# Revit family: Light_Fixture-Wall_Sconce-KOHLER-Holt-K-38414_1
name_source: partatom
category: Lighting Fixtures
units: mm (PartAtom-declared; Revit-internal decimal feet)

## family parameters
Cut with Voids When Loaded = No
Host = Face
Light Source = Yes
OmniClass Number = 23.35.47.11
OmniClass Title = Lighting Fixtures
Part Type = Normal
Room Calculation Point = No
Round Connector Dimension = Use Diameter
Shared = No

## types (3) — shared parameters
ADA Compliant = No
Apparent Load = 180 VA
Assembly Code = D5040.50
Color Filter = 16777215
Date Modified = 04/05/2023
Default Elevation = 60"
Description = Madera Globe 3-Light Sconce
Dimming Lamp Color Temperature Shift = Incandescent Lamp Curve
Electrical Connector = Yes
Electrical Note = One Dedicated Cicuit Required
Hardware Included = No
Height = 9 3/4"
Lamp = 3*E26 Type A 60W
Length = 23 15/16"
Light Source Symbol Size = 3"
Manufacturer = Kohler Co.
Master Format 2014 = 26 51 13
Master Format 2014 Name = Interior Lighting Fixtures, Lamps, And Ballasts
Material = Premium Metal Construction
Product Documentation Link = https://www.us.kohler.com
Product Name = Holt
Product Page URL = http://www.us.kohler.com
URL = https://www.us.kohler.com
Voltage = 120 V
WaterSense Certified = No
Wattage Comments = 180 W
Width = 6 13/16"

## per-type parameters (varying)
| type | Finish | Model | Secondary Finish | Tube Finish | Type |
| CPL-Polished Chrome | KOHLER-Metal-CPL-Polished_Chrome | K-38414-SC03-CPL | KOHLER-Metal-CPL-Polished_Chrome | Kohler-Wood-WSW-White_Stain_Wood | 1 |
| BNL-Brushed Nickel | KOHLER-Metal-BNL-Brushed_Nickel | K-38414-SC03-BNL | KOHLER-Metal-BNL-Brushed_Nickel | Kohler-Wood-1WE-Terry_Walnut | 2 |
| BML-Matte Black With Brushed Modern Brass | KOHLER-Metal-BLL-Matte_Black | K-38414-SC03-BML | KOHLER-Metal-2GL-Brushed_Modern_Brass | Kohler-Wood-1WE-Terry_Walnut | 3 |

## geometry (parser evidence)
native form markers: Sweep x7
no freeform markers — native parametric forms only
